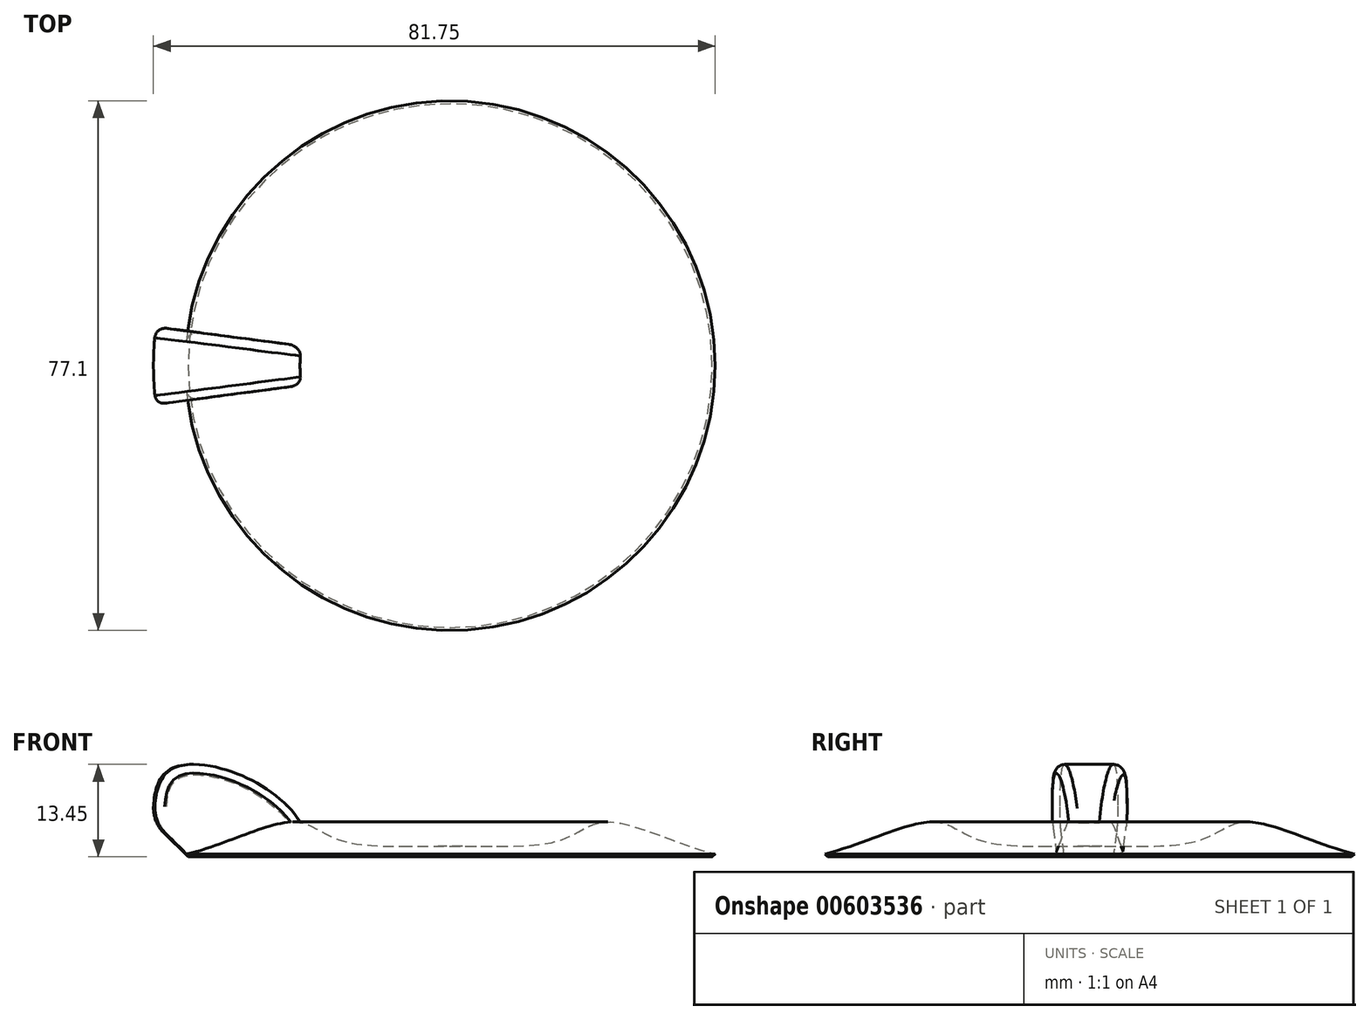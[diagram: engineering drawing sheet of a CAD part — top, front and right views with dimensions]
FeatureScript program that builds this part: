
annotation { "Feature Type Name" : "Feature", "Feature Type Description" : "" }
export const myFeature = defineFeature(function(context is Context, id is Id, definition is map)
    precondition{}
    {
        {
            var Q0;
            Q0=qCreatedBy(makeId("Front.planeOp"),FACE);
            var sketch = newSketch(context, id + "F0", { "sketchPlane" : qUnion([Q0])});
            skLineSegment(sketch, "E0", {"start": v(0, 0) * mm, "end": v(40.64, 0) * mm});
            skLineSegment(sketch, "E1", {"start": v(0, 0) * mm, "end": v(0, 1.52) * mm});
            skFitSpline(sketch, "E2", {"points": [v(0, 1.52) * mm, v(15.8, 2.34) * mm, v(22.86, 5.08) * mm, v(40.64, 0) * mm], "startDerivative": vector(32.15, 1.45) * mm, "endDerivative": vector(45.48, -6.3) * mm});
            skSolve(sketch);
        }
        {
            var Q0;
            Q0=makeQuery(id+"F0.imprint","IMPRINT",FACE,{"disambiguationData":[TD([[makeQuery(id+"F0.imprint","IMPRINT",EDGE,{"derivedFrom":sQuery(id+"F0.wireOp",EDGE,"E0")}),1.0]])]});
            var Q1;
            Q1=sQuery(id+"F0.wireOp",EDGE,"E1");
            revolve(context, id + "F1", {"entities" : qUnion([Q0]), "axis" : qUnion([Q1]), "revolveType" : RevolveType.FULL});
        }
        {
            var Q0;
            Q0=qCreatedBy(makeId("Front.planeOp"),FACE);
            var sketch = newSketch(context, id + "F2", { "sketchPlane" : qUnion([Q0])});
            skLineSegment(sketch, "E3", {"start": v(-20.32, 0) * mm, "end": v(-43.18, 0) * mm});
            skLineSegment(sketch, "E4", {"start": v(-43.18, 0) * mm, "end": v(-43.18, 3.82) * mm});
            skFitSpline(sketch, "E5", {"points": [v(-43.18, 3.82) * mm, v(-40.29, 12.97) * mm, v(-20.32, 0) * mm], "startDerivative": vector(-0.51, 23.07) * mm, "endDerivative": vector(0.69, -45.3) * mm});
            skLineSegment(sketch, "E6", {"start": v(0, 21.42) * mm, "end": v(0, 47.37) * mm, "construction": true});
            skSolve(sketch);
        }
        {
            var Q0;
            Q0=makeQuery(id+"F2.imprint","IMPRINT",FACE,{"disambiguationData":[TD([[makeQuery(id+"F2.imprint","IMPRINT",EDGE,{"derivedFrom":sQuery(id+"F2.wireOp",EDGE,"E3")}),-1.0]])]});
            var Q1;
            Q1=sQuery(id+"F2.wireOp",EDGE,"E6");
            revolve(context, id + "F3", {"operationType" : NewBodyOperationType.ADD, "entities" : qUnion([Q0]), "axis" : qUnion([Q1]), "revolveType" : RevolveType.SYMMETRIC, "angle" : 15 * degree});
        }
        {
            var Q0;
            Q0=makeQuery(id+"F3.opRevolve","SWEPT_EDGE",EDGE,{"disambiguationData":[OSD([sQuery(id+"F2.wireOp",EDGE,"E3"),sQuery(id+"F2.wireOp",EDGE,"E4")])]});
            chamfer(context, id + "F4", {"entities" : qUnion([Q0]), "width" : 5.08 * mm, "tangentPropagation" : true});
        }
        {
            var Q0;
            Q0=makeQuery(id+"F4.opChamfer","BLEND_EDGE",EDGE,{"blendedFrom":[makeQuery(id+"F3.opRevolve","SWEPT_EDGE",EDGE,{"disambiguationData":[OSD([sQuery(id+"F2.wireOp",EDGE,"E3"),sQuery(id+"F2.wireOp",EDGE,"E4")])]}),makeQuery(id+"F3.opRevolve","SWEPT_FACE",FACE,{"disambiguationData":[OSD([sQuery(id+"F2.wireOp",EDGE,"E5")])]})],"blendedInto":[makeQuery(id+"F3.opRevolve","SWEPT_FACE",FACE,{"disambiguationData":[OSD([sQuery(id+"F2.wireOp",EDGE,"E5")])]})]});
            fillet(context, id + "F5", {"entities" : qUnion([Q0]), "radius" : 5.08 * mm, "tangentPropagation" : true, "allowEdgeOverflow" : false});
        }
        {
            var Q0;
            Q0=makeQuery(id+"F3.opRevolve","CAP_EDGE",EDGE,{"disambiguationData":[OSD([sQuery(id+"F2.wireOp",EDGE,"E5")])],"isStart":true});
            var Q1;
            {var subQ0=sQuery(id+"F2.wireOp",EDGE,"E5");var subQ1=sQuery(id+"F2.wireOp",EDGE,"E4");var subQ2=sQuery(id+"F2.wireOp",EDGE,"E3");Q1=makeQuery(id+"F5.opFillet","BLEND_EDGE",EDGE,{"blendedFrom":[makeQuery(id+"F4.opChamfer","BLEND_EDGE",EDGE,{"blendedFrom":[makeQuery(id+"F3.opRevolve","SWEPT_EDGE",EDGE,{"disambiguationData":[OSD([subQ2,subQ1])]}),makeQuery(id+"F3.opRevolve","SWEPT_FACE",FACE,{"disambiguationData":[OSD([subQ0])]})],"blendedInto":[makeQuery(id+"F3.opRevolve","SWEPT_FACE",FACE,{"disambiguationData":[OSD([subQ0])]})]}),makeQuery(id+"F3.opRevolve","CAP_FACE",FACE,{"disambiguationData":[OSD([subQ2,subQ1,subQ0])],"isStart":true})],"blendedInto":[makeQuery(id+"F3.opRevolve","CAP_FACE",FACE,{"disambiguationData":[OSD([subQ2,subQ1,subQ0])],"isStart":true})]});}
            fillet(context, id + "F6", {"entities" : qUnion([Q0, Q1]), "radius" : 1.52 * mm, "tangentPropagation" : true, "allowEdgeOverflow" : false});
        }
        {
            var Q0;
            Q0=makeQuery(id+"F3.opRevolve","CAP_EDGE",EDGE,{"disambiguationData":[OSD([sQuery(id+"F2.wireOp",EDGE,"E5")])],"isStart":false});
            var Q1;
            {var subQ0=sQuery(id+"F2.wireOp",EDGE,"E5");var subQ1=sQuery(id+"F2.wireOp",EDGE,"E4");var subQ2=sQuery(id+"F2.wireOp",EDGE,"E3");Q1=makeQuery(id+"F5.opFillet","BLEND_EDGE",EDGE,{"blendedFrom":[makeQuery(id+"F4.opChamfer","BLEND_EDGE",EDGE,{"blendedFrom":[makeQuery(id+"F3.opRevolve","SWEPT_EDGE",EDGE,{"disambiguationData":[OSD([subQ2,subQ1])]}),makeQuery(id+"F3.opRevolve","SWEPT_FACE",FACE,{"disambiguationData":[OSD([subQ0])]})],"blendedInto":[makeQuery(id+"F3.opRevolve","SWEPT_FACE",FACE,{"disambiguationData":[OSD([subQ0])]})]}),makeQuery(id+"F3.opRevolve","CAP_FACE",FACE,{"disambiguationData":[OSD([subQ2,subQ1,subQ0])],"isStart":false})],"blendedInto":[makeQuery(id+"F3.opRevolve","CAP_FACE",FACE,{"disambiguationData":[OSD([subQ2,subQ1,subQ0])],"isStart":false})]});}
            fillet(context, id + "F7", {"entities" : qUnion([Q0, Q1]), "radius" : 1.27 * mm, "tangentPropagation" : true, "allowEdgeOverflow" : false});
        }
    });
